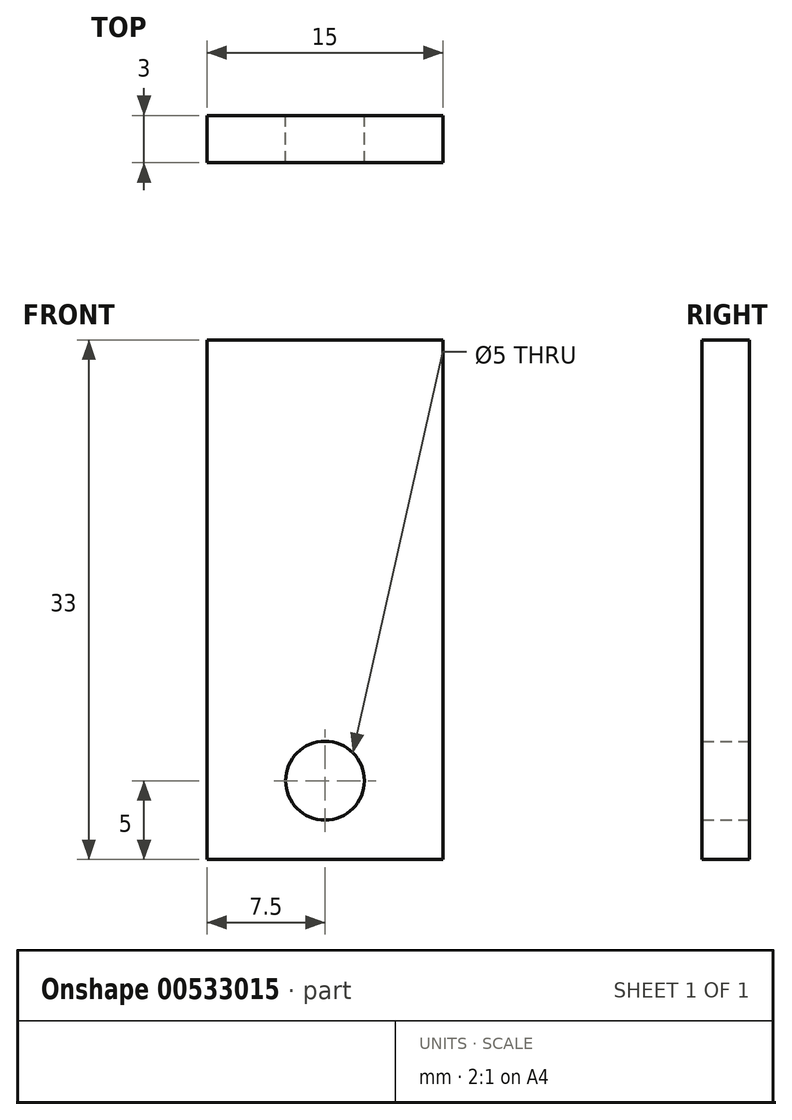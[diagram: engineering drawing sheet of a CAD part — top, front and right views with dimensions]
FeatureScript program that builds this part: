
annotation { "Feature Type Name" : "Feature", "Feature Type Description" : "" }
export const myFeature = defineFeature(function(context is Context, id is Id, definition is map)
    precondition{}
    {
        {
            var Q0;
            Q0=qCreatedBy(makeId("Front.planeOp"),FACE);
            var sketch = newSketch(context, id + "F0", { "sketchPlane" : qUnion([Q0])});
            skLineSegment(sketch, "E0.bottom", {"start": v(7.5, -16.5) * mm, "end": v(-7.5, -16.5) * mm});
            skLineSegment(sketch, "E0.top", {"start": v(7.5, 16.5) * mm, "end": v(-7.5, 16.5) * mm});
            skLineSegment(sketch, "E0.left", {"start": v(7.5, -16.5) * mm, "end": v(7.5, 16.5) * mm});
            skLineSegment(sketch, "E0.right", {"start": v(-7.5, -16.5) * mm, "end": v(-7.5, 16.5) * mm});
            skPoint(sketch, "E0.middle", {"position": v(0, 0) * mm});
            skCircle(sketch, "E1", {"center": v(0, -11.5) * mm, "radius": 2.5 * mm});
            skPoint(sketch, "E1.centerSnap0", {"position": v(0, -16.5) * mm});
            skSolve(sketch);
        }
        {
            var Q0;
            Q0=makeQuery(id+"F0.imprint","IMPRINT",FACE,{"disambiguationData":[TD([[makeQuery(id+"F0.imprint","IMPRINT",EDGE,{"derivedFrom":sQuery(id+"F0.wireOp",EDGE,"E0.bottom")}),-1.0]])]});
            extrude(context, id + "F1", {"entities" : qUnion([Q0]), "depth" : 3 * mm, "offsetDistance" : 25 * mm});
        }
    });
